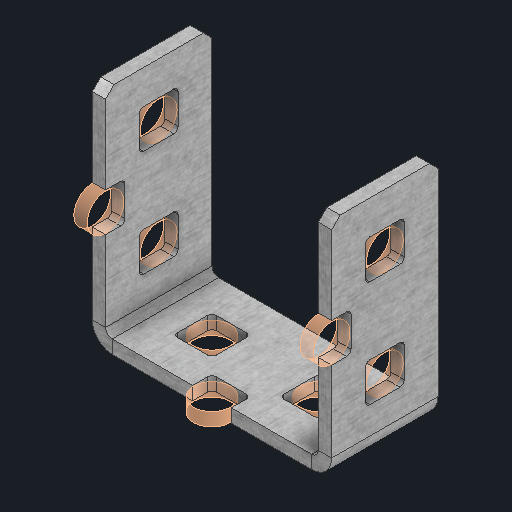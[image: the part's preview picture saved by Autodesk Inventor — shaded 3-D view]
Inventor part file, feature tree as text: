
AUTODESK INVENTOR PART (.ipt)
format: ipt  version: 2025 (Build 290162000, 162)  size: 468,480 bytes
history: native  units: in
note: dims shown in document units (in); Inventor stores cm internally (conversion verified against a paired STEP export)
features: other x173, sketch x2, sheet_metal_op x1
ambient origin geometry x8: Origin, YZ Plane, XZ Plane, XY Plane, X Axis, Y Axis, Z Axis, Center Point
bodies: Solid1 (feature_tree)
feature tree (176):
  other  "Alu C 2x2x2x1.ipt"
  other  "Solid1::Alu C 2x2x2x1.ipt"
  other  "TaggingFeature1"
  sketch  "Sketch1"  dims[d0=0.3937in]
  sketch  "Sketch2"  dims[d1=0.0625in]
  sheet_metal_op  "Body Pattern Sketch"
  other  "Arc Length"
  other  "Diagonal Plane"
  other  "Srf1"
  other  "Srf2"
  other  "Srf3"
  other  "Srf4"
  other  "Srf5"
  other  "Srf6"
  other  "Srf7"
  other  "Srf8"
  other  "Srf9"
  other  "Srf10"
  other  "Srf11"
  other  "Srf12"
  other  "Srf13"
  other  "Srf14"
  other  "Srf15"
  other  "Srf16"
  other  "Srf17"
  other  "Srf18"
  other  "Srf19"
  other  "Srf20"
  other  "Srf21"
  other  "Srf22"
  other  "Srf23"
  other  "Srf24"
  other  "Srf25"
  other  "Srf26"
  other  "Srf27"
  other  "Srf28"
  other  "Srf29"
  other  "Srf30"
  other  "Srf31"
  other  "Srf32"
  other  "Srf33"
  other  "Srf34"
  other  "Srf35"
  other  "Srf36"
  other  "Srf37"
  other  "Srf38"
  other  "Srf39"
  other  "Srf40"
  other  "Srf41"
  other  "Srf42"
  other  "Srf43"
  other  "Srf44"
  other  "Srf45"
  other  "Srf46"
  other  "Srf47"
  other  "Srf48"
  other  "Srf49"
  other  "Srf50"
  other  "Srf51"
  other  "Srf52"
  other  "Srf53"
  other  "Srf54"
  other  "Srf55"
  other  "Srf56"
  other  "Srf57"
  other  "Srf58"
  other  "Srf59"
  other  "Srf60"
  other  "Srf61"
  other  "Srf62"
  other  "Srf63"
  other  "Srf64"
  other  "Srf65"
  other  "Srf66"
  other  "Srf67"
  other  "Srf68"
  other  "Srf69"
  other  "Srf70"
  other  "Srf71"
  other  "Srf72"
  other  "Srf73"
  other  "Srf74"
  other  "Srf75"
  other  "Srf76"
  other  "Srf77"
  other  "Srf78"
  other  "Srf79"
  other  "Srf80"
  other  "Srf81"
  other  "Srf82"
  other  "Srf83"
  other  "Srf84"
  other  "Srf91::Derived"
  other  "Srf92::Derived"
  other  "Srf786::Derived"
  other  "Srf889::Derived"
  other  "Srf890::Derived"
  other  "Srf891::Derived"
  other  "Srf892::Derived"
  other  "Srf893::Derived"
  other  "Srf894::Derived"
  other  "Srf895::Derived"
  other  "Srf896::Derived"
  other  "Srf996::Derived"
  other  "Srf997::Derived"
  other  "Srf998::Derived"
  other  "Srf999::Derived"
  other  "Srf1000::Derived"
  other  "Srf1255::Derived"
  other  "Srf1256::Derived"
  other  "Srf1257::Derived"
  other  "Srf1258::Derived"
  other  "Srf1259::Derived"
  other  "Srf1315::Derived"
  other  "Srf1316::Derived"
  other  "Srf1317::Derived"
  other  "Srf1325::Derived"
  other  "Srf1326::Derived"
  other  "Srf1327::Derived"
  other  "Srf1328::Derived"
  other  "Srf1329::Derived"
  other  "Srf1330::Derived"
  other  "Srf1331::Derived"
  other  "Srf1332::Derived"
  other  "Srf1338::Derived"
  other  "Srf1339::Derived"
  other  "Srf1340::Derived"
  other  "Srf1341::Derived"
  other  "Srf1342::Derived"
  other  "Srf1369::Derived"
  other  "Srf1370::Derived"
  other  "Srf1371::Derived"
  other  "Srf1372::Derived"
  other  "Srf1373::Derived"
  other  "Srf1374::Derived"
  other  "Srf1375::Derived"
  other  "Srf1376::Derived"
  other  "Srf1384::Derived"
  other  "Srf1385::Derived"
  other  "Srf1386::Derived"
  other  "Srf1387::Derived"
  other  "Srf1388::Derived"
  other  "Srf1389::Derived"
  other  "Srf1390::Derived"
  other  "Srf1391::Derived"
  other  "Srf1397::Derived"
  other  "Srf1398::Derived"
  other  "Srf1399::Derived"
  other  "Srf1400::Derived"
  other  "Srf1401::Derived"
  other  "Srf1428::Derived"
  other  "Srf1429::Derived"
  other  "Srf1430::Derived"
  other  "Srf1431::Derived"
  other  "Srf1432::Derived"
  other  "Srf1433::Derived"
  other  "Srf1434::Derived"
  other  "Srf1473::Derived"
  other  "Srf1474::Derived"
  other  "Srf1475::Derived"
  other  "Srf1476::Derived"
  other  "Srf1477::Derived"
  other  "Srf1478::Derived"
  other  "Srf1479::Derived"
  other  "Srf1480::Derived"
  other  "Srf1481::Derived"
  other  "Srf1482::Derived"
  other  "Srf1483::Derived"
  other  "Srf1484::Derived"
  other  "Srf1485::Derived"
  other  "Srf1486::Derived"
  other  "Srf1487::Derived"
  other  "Srf1488::Derived"
  other  "Srf1489::Derived"
  other  "Srf1490::Derived"
  other  "Srf1491::Derived"
